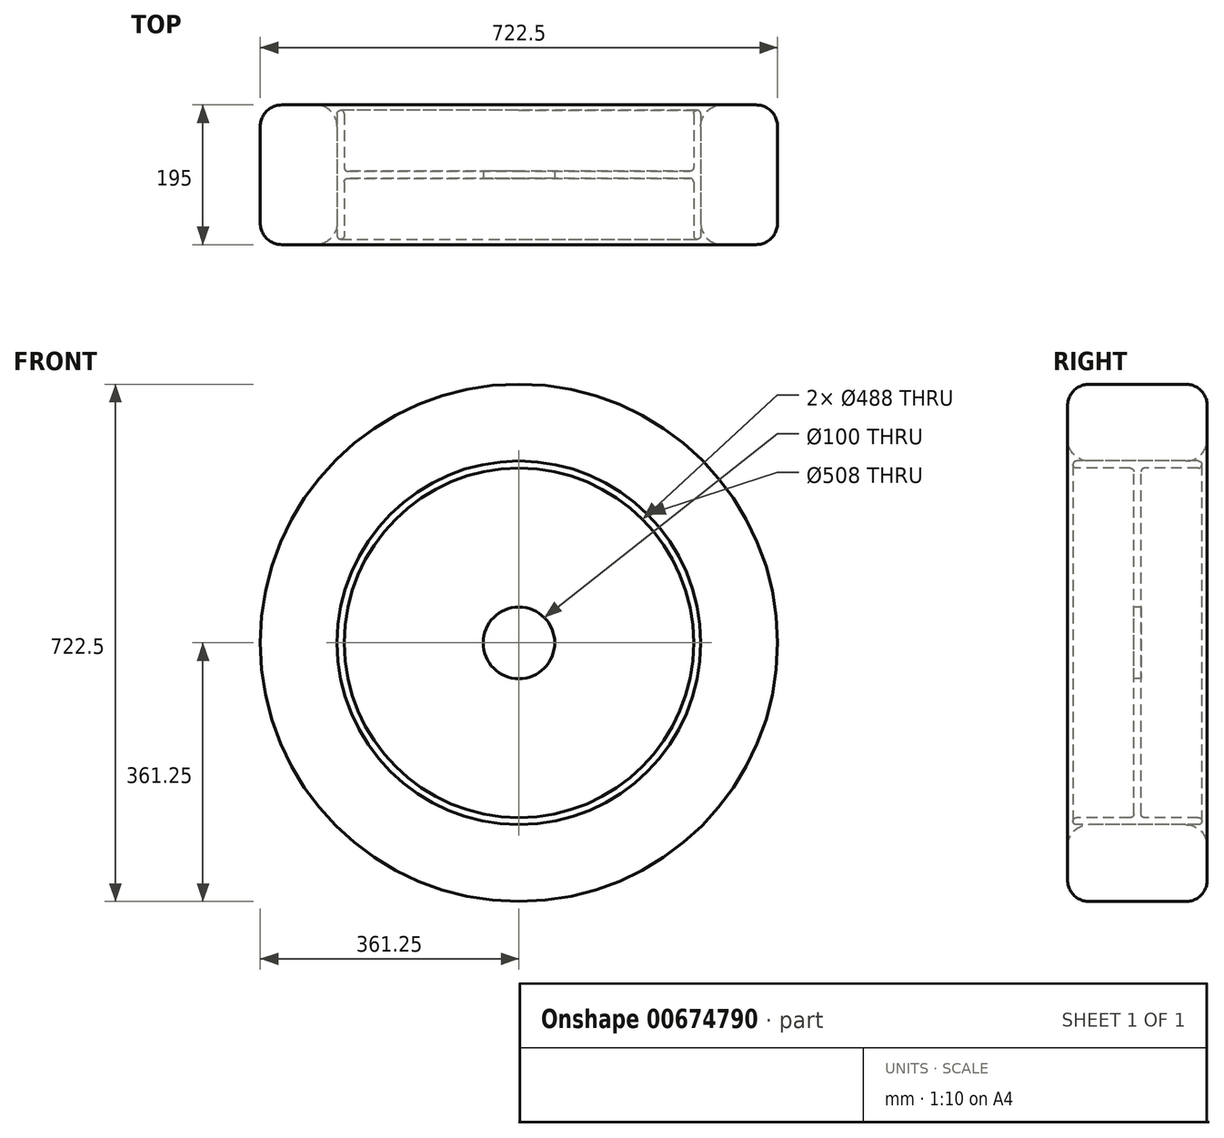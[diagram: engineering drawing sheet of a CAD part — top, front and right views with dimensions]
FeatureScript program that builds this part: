
annotation { "Feature Type Name" : "Feature", "Feature Type Description" : "" }
export const myFeature = defineFeature(function(context is Context, id is Id, definition is map)
    precondition{}
    {
        {
            var Q0;
            Q0=qCreatedBy(makeId("Right.planeOp"),FACE);
            var sketch = newSketch(context, id + "F0", { "sketchPlane" : qUnion([Q0])});
            skLineSegment(sketch, "E0.bottom", {"start": v(-67.5, 361.25) * mm, "end": v(67.5, 361.25) * mm});
            skLineSegment(sketch, "E0.top", {"start": v(-67.5, 254) * mm, "end": v(67.5, 254) * mm});
            skLineSegment(sketch, "E0.left", {"start": v(-97.5, 331.25) * mm, "end": v(-97.5, 284) * mm});
            skLineSegment(sketch, "E0.right", {"start": v(97.5, 331.25) * mm, "end": v(97.5, 284) * mm});
            skPoint(sketch, "E1.visualSharp", {"position": v(-97.5, 361.25) * mm});
            skArc(sketch, "E1.filletArc", {"start": v(-67.5, 361.25) * mm, "mid": v(-88.71, 352.46) * mm, "end": v(-97.5, 331.25) * mm});
            skPoint(sketch, "E2.visualSharp", {"position": v(97.5, 361.25) * mm});
            skArc(sketch, "E2.filletArc", {"start": v(97.5, 331.25) * mm, "mid": v(88.71, 352.46) * mm, "end": v(67.5, 361.25) * mm});
            skPoint(sketch, "E3.visualSharp", {"position": v(97.5, 254) * mm});
            skArc(sketch, "E3.filletArc", {"start": v(67.5, 254) * mm, "mid": v(88.71, 262.79) * mm, "end": v(97.5, 284) * mm});
            skPoint(sketch, "E4.visualSharp", {"position": v(-97.5, 254) * mm});
            skArc(sketch, "E4.filletArc", {"start": v(-97.5, 284) * mm, "mid": v(-88.71, 262.79) * mm, "end": v(-67.5, 254) * mm});
            skSolve(sketch);
        }
        {
            var Q0;
            Q0=qCreatedBy(makeId("Front.planeOp"),FACE);
            var sketch = newSketch(context, id + "F1", { "sketchPlane" : qUnion([Q0])});
            skLineSegment(sketch, "E5.bottom", {"start": v(-47.5, 361.25) * mm, "end": v(47.5, 361.25) * mm});
            skLineSegment(sketch, "E5.top", {"start": v(-47.5, 254) * mm, "end": v(47.5, 254) * mm});
            skLineSegment(sketch, "E5.left", {"start": v(-97.5, 311.25) * mm, "end": v(-97.5, 304) * mm});
            skLineSegment(sketch, "E5.right", {"start": v(97.5, 311.25) * mm, "end": v(97.5, 304) * mm});
            skPoint(sketch, "E6.visualSharp", {"position": v(-97.5, 361.25) * mm});
            skArc(sketch, "E6.filletArc", {"start": v(-47.5, 361.25) * mm, "mid": v(-82.86, 346.6) * mm, "end": v(-97.5, 311.25) * mm});
            skPoint(sketch, "E7.visualSharp", {"position": v(-97.5, 254) * mm});
            skArc(sketch, "E7.filletArc", {"start": v(-97.5, 304) * mm, "mid": v(-82.86, 268.64) * mm, "end": v(-47.5, 254) * mm});
            skPoint(sketch, "E8.visualSharp", {"position": v(97.5, 254) * mm});
            skArc(sketch, "E8.filletArc", {"start": v(47.5, 254) * mm, "mid": v(82.86, 268.64) * mm, "end": v(97.5, 304) * mm});
            skPoint(sketch, "E9.visualSharp", {"position": v(97.5, 361.25) * mm});
            skArc(sketch, "E9.filletArc", {"start": v(97.5, 311.25) * mm, "mid": v(82.86, 346.6) * mm, "end": v(47.5, 361.25) * mm});
            skLineSegment(sketch, "E10.bottom", {"start": v(-70, 254) * mm, "end": v(70, 254) * mm});
            skLineSegment(sketch, "E10.top", {"start": v(-70, 234) * mm, "end": v(70, 234) * mm});
            skLineSegment(sketch, "E10.left", {"start": v(-80, 244) * mm, "end": v(-80, 244) * mm});
            skLineSegment(sketch, "E10.right", {"start": v(80, 244) * mm, "end": v(80, 244) * mm});
            skPoint(sketch, "E11.visualSharp", {"position": v(-80, 234) * mm});
            skArc(sketch, "E11.filletArc", {"start": v(-80, 244) * mm, "mid": v(-77.07, 236.93) * mm, "end": v(-70, 234) * mm});
            skPoint(sketch, "E12.visualSharp", {"position": v(80, 234) * mm});
            skArc(sketch, "E12.filletArc", {"start": v(70, 234) * mm, "mid": v(77.07, 236.93) * mm, "end": v(80, 244) * mm});
            skPoint(sketch, "E13.visualSharp", {"position": v(80, 254) * mm});
            skArc(sketch, "E13.filletArc", {"start": v(80, 244) * mm, "mid": v(77.07, 251.07) * mm, "end": v(70, 254) * mm});
            skPoint(sketch, "E14.visualSharp", {"position": v(-80, 254) * mm});
            skArc(sketch, "E14.filletArc", {"start": v(-70, 254) * mm, "mid": v(-77.07, 251.07) * mm, "end": v(-80, 244) * mm});
            skLineSegment(sketch, "E15.bottom", {"start": v(-12.34, 234) * mm, "end": v(16.8, 234) * mm});
            skLineSegment(sketch, "E15.top", {"start": v(-12.34, 0) * mm, "end": v(16.8, 0) * mm});
            skLineSegment(sketch, "E15.left", {"start": v(-12.34, 234) * mm, "end": v(-12.34, 0) * mm});
            skLineSegment(sketch, "E15.right", {"start": v(16.8, 234) * mm, "end": v(16.8, 0) * mm});
            skSolve(sketch);
        }
        {
            var Q0;
            Q0=qCreatedBy(makeId("Right.planeOp"),FACE);
            var sketch = newSketch(context, id + "F2", { "sketchPlane" : qUnion([Q0])});
            skLineSegment(sketch, "E16.bottom", {"start": v(-85, 254) * mm, "end": v(85, 254) * mm});
            skLineSegment(sketch, "E16.top", {"start": v(-85, 244) * mm, "end": v(-10, 244) * mm});
            skLineSegment(sketch, "E16.left", {"start": v(-90, 249) * mm, "end": v(-90, 249) * mm});
            skLineSegment(sketch, "E16.right", {"start": v(90, 249) * mm, "end": v(90, 249) * mm});
            skPoint(sketch, "E17.visualSharp", {"position": v(-90, 254) * mm});
            skArc(sketch, "E17.filletArc", {"start": v(-85, 254) * mm, "mid": v(-88.54, 252.54) * mm, "end": v(-90, 249) * mm});
            skPoint(sketch, "E18.visualSharp", {"position": v(-90, 244) * mm});
            skArc(sketch, "E18.filletArc", {"start": v(-90, 249) * mm, "mid": v(-88.54, 245.46) * mm, "end": v(-85, 244) * mm});
            skPoint(sketch, "E19.visualSharp", {"position": v(90, 254) * mm});
            skArc(sketch, "E19.filletArc", {"start": v(90, 249) * mm, "mid": v(88.54, 252.54) * mm, "end": v(85, 254) * mm});
            skPoint(sketch, "E20.visualSharp", {"position": v(90, 244) * mm});
            skArc(sketch, "E20.filletArc", {"start": v(85, 244) * mm, "mid": v(88.54, 245.46) * mm, "end": v(90, 249) * mm});
            skLineSegment(sketch, "E21.top", {"start": v(-5, 0) * mm, "end": v(5, 0) * mm});
            skLineSegment(sketch, "E21.left", {"start": v(-5, 239) * mm, "end": v(-5, 0) * mm});
            skLineSegment(sketch, "E21.right", {"start": v(5, 239) * mm, "end": v(5, 0) * mm});
            skLineSegment(sketch, "E22.trimOffspring", {"start": v(10, 244) * mm, "end": v(85, 244) * mm});
            skPoint(sketch, "E23.visualSharp", {"position": v(-5, 244) * mm});
            skArc(sketch, "E23.filletArc", {"start": v(-5, 239) * mm, "mid": v(-6.46, 242.54) * mm, "end": v(-10, 244) * mm});
            skPoint(sketch, "E24.visualSharp", {"position": v(5, 244) * mm});
            skArc(sketch, "E24.filletArc", {"start": v(10, 244) * mm, "mid": v(6.46, 242.54) * mm, "end": v(5, 239) * mm});
            skSolve(sketch);
        }
        {
            var Q0;
            Q0=makeQuery(id+"F0.imprint","IMPRINT",FACE,{"disambiguationData":[TD([[makeQuery(id+"F0.imprint","IMPRINT",EDGE,{"derivedFrom":sQuery(id+"F0.wireOp",EDGE,"E0.bottom")}),-1.0]])]});
            var Q1;
            Q1=sQuery(id+"F2.wireOp",EDGE,"E21.top");
            revolve(context, id + "F3", {"entities" : qUnion([Q0]), "axis" : qUnion([Q1]), "revolveType" : RevolveType.FULL});
        }
        {
            var Q0;
            Q0=makeQuery(id+"F2.imprint","IMPRINT",FACE,{"disambiguationData":[TD([[makeQuery(id+"F2.imprint","IMPRINT",EDGE,{"derivedFrom":sQuery(id+"F2.wireOp",EDGE,"E16.bottom")}),-1.0]])]});
            var Q1;
            Q1=sQuery(id+"F2.wireOp",EDGE,"E21.top");
            revolve(context, id + "F4", {"entities" : qUnion([Q0]), "axis" : qUnion([Q1]), "revolveType" : RevolveType.FULL});
        }
        {
            var Q0;
            Q0=makeQuery(id+"F4.opRevolve","SWEPT_FACE",FACE,{"disambiguationData":[OSD([sQuery(id+"F2.wireOp",EDGE,"E21.left")])]});
            var sketch = newSketch(context, id + "F5", { "sketchPlane" : qUnion([Q0])});
            skCircle(sketch, "E25", {"center": v(0, 0) * mm, "radius": 50 * mm});
            skSolve(sketch);
        }
        {
            var Q0;
            Q0=makeQuery(id+"F5.imprint","IMPRINT",FACE,{"disambiguationData":[TD([[makeQuery(id+"F5.imprint","IMPRINT",EDGE,{"derivedFrom":sQuery(id+"F5.wireOp",EDGE,"E25")}),1.0]])]});
            extrude(context, id + "F6", {"entities" : qUnion([Q0]), "operationType" : NewBodyOperationType.REMOVE, "oppositeDirection" : true, "depth" : 25 * mm, "offsetDistance" : 25 * mm});
        }
    });
